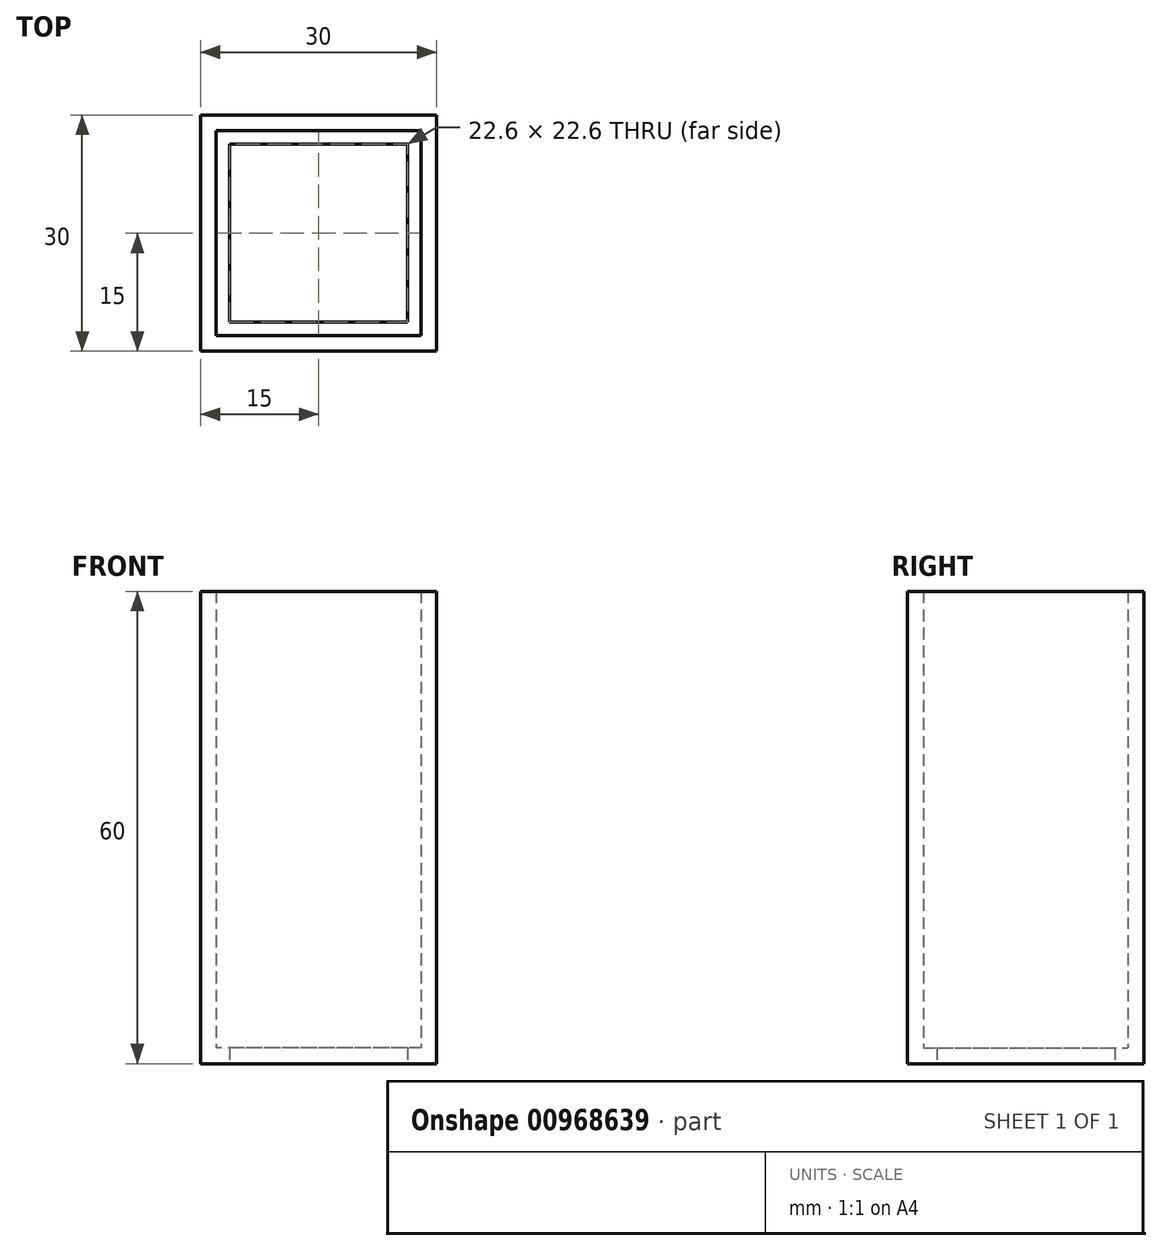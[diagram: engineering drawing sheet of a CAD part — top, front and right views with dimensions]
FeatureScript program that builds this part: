
annotation { "Feature Type Name" : "Feature", "Feature Type Description" : "" }
export const myFeature = defineFeature(function(context is Context, id is Id, definition is map)
    precondition{}
    {
        {
            var Q0;
            Q0=qCreatedBy(makeId("Top.planeOp"),FACE);
            var sketch = newSketch(context, id + "F0", { "sketchPlane" : qUnion([Q0])});
            skLineSegment(sketch, "E0.bottom", {"start": v(15, -15) * mm, "end": v(-15, -15) * mm});
            skLineSegment(sketch, "E0.top", {"start": v(15, 15) * mm, "end": v(-15, 15) * mm});
            skLineSegment(sketch, "E0.left", {"start": v(15, -15) * mm, "end": v(15, 15) * mm});
            skLineSegment(sketch, "E0.right", {"start": v(-15, -15) * mm, "end": v(-15, 15) * mm});
            skPoint(sketch, "E0.middle", {"position": v(0, 0) * mm});
            skLineSegment(sketch, "E1.0", {"start": v(11.3, -11.3) * mm, "end": v(11.3, 11.3) * mm});
            skLineSegment(sketch, "E1.1", {"start": v(11.3, -11.3) * mm, "end": v(-11.3, -11.3) * mm});
            skLineSegment(sketch, "E1.2", {"start": v(-11.3, -11.3) * mm, "end": v(-11.3, 11.3) * mm});
            skLineSegment(sketch, "E1.3", {"start": v(11.3, 11.3) * mm, "end": v(-11.3, 11.3) * mm});
            skLineSegment(sketch, "E2.0", {"start": v(-13, -13) * mm, "end": v(-13, 13) * mm});
            skLineSegment(sketch, "E2.1", {"start": v(13, -13) * mm, "end": v(-13, -13) * mm});
            skLineSegment(sketch, "E2.2", {"start": v(13, -13) * mm, "end": v(13, 13) * mm});
            skLineSegment(sketch, "E2.3", {"start": v(13, 13) * mm, "end": v(-13, 13) * mm});
            skSolve(sketch);
        }
        {
            var Q0;
            Q0=makeQuery(id+"F0.imprint","IMPRINT",FACE,{"disambiguationData":[TD([[makeQuery(id+"F0.imprint","IMPRINT",EDGE,{"derivedFrom":sQuery(id+"F0.wireOp",EDGE,"E0.bottom")}),-1.0]])]});
            extrude(context, id + "F1", {"entities" : qUnion([Q0]), "depth" : 60 * mm, "offsetDistance" : 25 * mm});
        }
        {
            var Q0;
            Q0=makeQuery(id+"F1.opExtrude","CAP_FACE",FACE,{"disambiguationData":[OSD([sQuery(id+"F0.wireOp",EDGE,"E0.bottom"),sQuery(id+"F0.wireOp",EDGE,"E0.top"),sQuery(id+"F0.wireOp",EDGE,"E0.left"),sQuery(id+"F0.wireOp",EDGE,"E0.right")])],"isStart":true});
            var sketch = newSketch(context, id + "F2", { "sketchPlane" : qUnion([Q0])});
            skCircle(sketch, "E3", {"center": v(0, 0) * mm, "radius": 2.5 * mm});
            skLineSegment(sketch, "E4.bottom", {"start": v(-2.5, -15) * mm, "end": v(2.5, -15) * mm});
            skLineSegment(sketch, "E4.top", {"start": v(-2.5, 15) * mm, "end": v(2.5, 15) * mm});
            skLineSegment(sketch, "E4.left", {"start": v(-2.5, -15) * mm, "end": v(-2.5, 15) * mm});
            skLineSegment(sketch, "E4.right", {"start": v(2.5, -15) * mm, "end": v(2.5, 15) * mm});
            skSolve(sketch);
        }
        {
            var Q0;
            {var subQ0=sQuery(id+"F2.wireOp",EDGE,"E3");var subQ1=makeQuery(id+"F2.imprint","INTERSECT",VERTEX,{"derivedFrom":[subQ0,sQuery(id+"F2.wireOp",EDGE,"E4.left")]});Q0=makeQuery(id+"F2.imprint","IMPRINT",FACE,{"disambiguationData":[TD([[makeQuery(id+"F2.imprint","IMPRINT",EDGE,{"disambiguationData":[TD([[subQ1,1.0]])],"derivedFrom":subQ0}),1.0]])]});}
            extrude(context, id + "F3", {"entities" : qUnion([Q0]), "operationType" : NewBodyOperationType.REMOVE, "oppositeDirection" : true, "depth" : 3 * mm, "offsetDistance" : 25 * mm});
        }
        {
            var Q0;
            Q0=makeQuery(id+"F0.imprint","IMPRINT",FACE,{"disambiguationData":[TD([[makeQuery(id+"F0.imprint","IMPRINT",EDGE,{"derivedFrom":sQuery(id+"F0.wireOp",EDGE,"E1.0")}),-1.0]])]});
            extrude(context, id + "F4", {"entities" : qUnion([Q0]), "operationType" : NewBodyOperationType.ADD, "depth" : 2 * mm, "offsetDistance" : 25 * mm});
        }
    });
